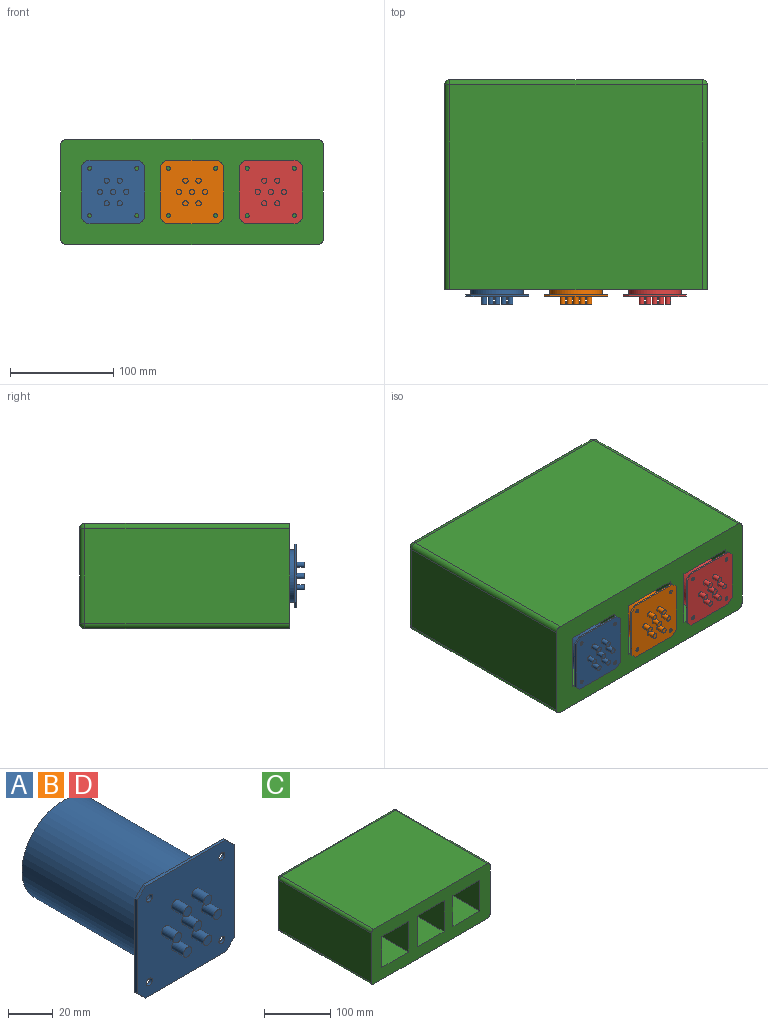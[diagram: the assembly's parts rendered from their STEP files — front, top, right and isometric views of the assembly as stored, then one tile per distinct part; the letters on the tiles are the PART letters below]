
ASSEMBLY  parts=4 mates=3
PART A: 30 faces, bbox 61x85.4x61 mm
  f0: plane 60.96x60.96mm, normal (0,-1,0), area 3477mm2, adj f4,f5,f6,f7,f8,f9,f10,f11
  f1: plane 60.96x60.96mm, normal (0,1,0), area 1592.1mm2, adj f2,f4,f5,f6,f7,f8,f9,f10
  f2: cylinder r=25.4mm len=76.2mm, axis (0,1,0), area 12161mm2, adj f1,f3
  f3: plane 50.8x50.8mm, normal (0,1,0), area 2026.8mm2, adj f2
  f4: plane 50.8x1.59mm, normal (0,0,1), area 80.6mm2, adj f0,f1,f9,f11
  f5: plane 50.8x1.59mm, normal (-1,0,0), area 80.6mm2, adj f0,f1,f8,f9
  f6: plane 50.8x1.59mm, normal (0,0,-1), area 80.6mm2, adj f0,f1,f8,f10
  f7: plane 50.8x1.59mm, normal (1,0,0), area 80.6mm2, adj f0,f1,f10,f11
  f8: plane 5.08x5.08mm, normal (-0.71,0,-0.71), area 11.4mm2, adj f0,f1,f5,f6
  f9: plane 5.08x5.08mm, normal (-0.71,0,0.71), area 11.4mm2, adj f0,f1,f4,f5
  f10: plane 5.08x5.08mm, normal (0.71,0,-0.71), area 11.4mm2, adj f0,f1,f6,f7
  f11: plane 5.08x5.08mm, normal (0.71,0,0.71), area 11.4mm2, adj f0,f1,f4,f7
  f12: cylinder r=2.54mm len=7.62mm, axis (0,1,0), area 121.6mm2, adj f0,f13
  f13: plane 5.08x5.08mm, normal (0,-1,0), area 20.3mm2, adj f12
  f14: cylinder r=2.54mm len=7.62mm, axis (0,1,0), area 121.6mm2, adj f0,f15
  f15: plane 5.08x5.08mm, normal (0,-1,0), area 20.3mm2, adj f14
  f16: cylinder r=2.54mm len=7.62mm, axis (0,1,0), area 121.6mm2, adj f0,f17
  f17: plane 5.08x5.08mm, normal (0,-1,0), area 20.3mm2, adj f16
  f18: cylinder r=2.54mm len=7.62mm, axis (0,1,0), area 121.6mm2, adj f0,f19
  f19: plane 5.08x5.08mm, normal (0,-1,0), area 20.3mm2, adj f18
  f20: cylinder r=2.54mm len=7.62mm, axis (0,1,0), area 121.6mm2, adj f0,f21
  f21: plane 5.08x5.08mm, normal (0,-1,0), area 20.3mm2, adj f20
  f22: cylinder r=2.54mm len=7.62mm, axis (0,1,0), area 121.6mm2, adj f0,f23
  f23: plane 5.08x5.08mm, normal (0,-1,0), area 20.3mm2, adj f22
  f24: cylinder r=2.54mm len=7.62mm, axis (0,1,0), area 121.6mm2, adj f0,f25
  f25: plane 5.08x5.08mm, normal (0,-1,0), area 20.3mm2, adj f24
  f26: cylinder r=1.91mm len=3.81mm, axis (0,-1,0), area 19mm2, adj f0,f1
  f27: cylinder r=1.91mm len=3.81mm, axis (0,-1,0), area 19mm2, adj f0,f1
  f28: cylinder r=1.91mm len=3.81mm, axis (0,-1,0), area 19mm2, adj f0,f1
  f29: cylinder r=1.91mm len=3.81mm, axis (0,-1,0), area 19mm2, adj f0,f1
PART B: same geometry as A
PART C: 39 faces, bbox 254x203.2x101.6 mm
  f0: plane 254x101.6mm, normal (0,-1,0), area 15985.9mm2, adj f1,f2,f4,f5,f6,f7,f8,f9
  f1: plane 198.12x91.44mm, normal (-1,0,0), area 18116.1mm2, adj f0,f24,f25,f27
  f2: plane 198.12x91.44mm, normal (1,0,0), area 18116.1mm2, adj f0,f22,f23,f31
  f3: plane 243.84x91.44mm, normal (0,1,0), area 22296.7mm2, adj f21,f27,f29,f31
  f4: plane 243.84x198.12mm, normal (0,0,1), area 48309.6mm2, adj f0,f23,f24,f29
  f5: plane 243.84x198.12mm, normal (0,0,-1), area 48309.6mm2, adj f0,f21,f22,f25
  f6: plane 76.2x57.15mm, normal (1,0,0), area 4354.8mm2, adj f0,f7,f9,f10
  f7: plane 76.2x57.15mm, normal (0,0,1), area 4354.8mm2, adj f0,f6,f8,f10
  f8: plane 76.2x57.15mm, normal (-1,0,0), area 4354.8mm2, adj f0,f7,f9,f10
  f9: plane 76.2x57.15mm, normal (0,0,-1), area 4354.8mm2, adj f0,f6,f8,f10
  f10: plane 57.15x57.15mm, normal (0,-1,0), area 2759.4mm2, adj f6,f7,f8,f9,f37
  f11: plane 76.2x57.15mm, normal (0,0,-1), area 4354.8mm2, adj f0,f12,f14,f15
  f12: plane 76.2x57.15mm, normal (1,0,0), area 4354.8mm2, adj f0,f11,f13,f15
  f13: plane 76.2x57.15mm, normal (0,0,1), area 4354.8mm2, adj f0,f12,f14,f15
  f14: plane 76.2x57.15mm, normal (-1,0,0), area 4354.8mm2, adj f0,f11,f13,f15
  f15: plane 57.15x57.15mm, normal (0,-1,0), area 2759.4mm2, adj f11,f12,f13,f14,f35
  f16: plane 76.2x57.15mm, normal (0,0,1), area 4354.8mm2, adj f0,f17,f19,f20
  f17: plane 76.2x57.15mm, normal (-1,0,0), area 4354.8mm2, adj f0,f16,f18,f20
  f18: plane 76.2x57.15mm, normal (0,0,-1), area 4354.8mm2, adj f0,f17,f19,f20
  f19: plane 76.2x57.15mm, normal (1,0,0), area 4354.8mm2, adj f0,f16,f18,f20
  f20: plane 57.15x57.15mm, normal (0,-1,0), area 2759.4mm2, adj f16,f17,f18,f19,f33
  f21: cylinder r=5.08mm len=243.84mm, axis (-1,0,0), area 1945.8mm2, adj f3,f5,f26,f32
  f22: cylinder r=5.08mm len=198.12mm, axis (0,1,0), area 1580.9mm2, adj f0,f2,f5,f32
  f23: cylinder r=5.08mm len=198.12mm, axis (0,-1,0), area 1580.9mm2, adj f0,f2,f4,f30
  f24: cylinder r=5.08mm len=198.12mm, axis (0,1,0), area 1580.9mm2, adj f0,f1,f4,f28
  f25: cylinder r=5.08mm len=198.12mm, axis (0,-1,0), area 1580.9mm2, adj f0,f1,f5,f26
  f26: sphere r=5.08mm, area 40.5mm2, adj f21,f25,f27
  f27: cylinder r=5.08mm len=91.44mm, axis (0,0,-1), area 729.7mm2, adj f1,f3,f26,f28
  f28: sphere r=5.08mm, area 40.5mm2, adj f24,f27,f29
  f29: cylinder r=5.08mm len=243.84mm, axis (1,0,0), area 1945.8mm2, adj f3,f4,f28,f30
  f30: sphere r=5.08mm, area 40.5mm2, adj f23,f29,f31
  f31: cylinder r=5.08mm len=91.44mm, axis (0,0,1), area 729.7mm2, adj f2,f3,f30,f32
  f32: sphere r=5.08mm, area 40.5mm2, adj f21,f22,f31
  f33: cylinder r=12.7mm len=25.4mm, axis (0,1,0), area 405.4mm2, adj f20,f34
  f34: plane 25.4x25.4mm, normal (0,-1,0), area 506.7mm2, adj f33
  f35: cylinder r=12.7mm len=25.4mm, axis (0,1,0), area 405.4mm2, adj f15,f36
  f36: plane 25.4x25.4mm, normal (0,-1,0), area 506.7mm2, adj f35
  f37: cylinder r=12.7mm len=25.4mm, axis (0,1,0), area 405.4mm2, adj f10,f38
  f38: plane 25.4x25.4mm, normal (0,-1,0), area 506.7mm2, adj f37
PART D: same geometry as A
PLACE A t=(-124.93,13.67,156.51)mm
PLACE B t=(-48.73,13.67,156.51)mm
PLACE C t=(-175.73,-57.45,105.71)mm
PLACE D t=(27.47,13.67,156.51)mm
MATE fastened A.f2 <-> C.f33  axis (0,1,0) through (-124.93,13.67,156.51)mm
MATE fastened D.f2 <-> C.f37  axis (0,1,0) through (27.47,13.67,156.51)mm
MATE fastened B.f2 <-> C.f35  axis (0,1,0) through (-48.73,13.67,156.51)mm
